# Revit family: Toilet-Elongated-Right_Height-American_Standard-Colony-221AB_Series
name_source: partatom
category: Plumbing Fixtures
revit_build: Autodesk Revit 2014 (Build: 20130308_1515(x64)
units: mm (PartAtom-declared; Revit-internal decimal feet)

## types (7) — shared parameters
ADA Compliant = Yes
Aquaguard Liner = No
Assembly Code = D2010110
Bowl Shape = Elongated
CW Connection = Yes
CWFU = 5
Cold Water Connection Diameter = 3/8"
Cold Water Connection Height = 10"
Cold Water Connection Radius = 3/16"
Cold Water Connection Width = 6"
Default Elevation = 0"
HW Connection = No
Height = 31"
Installation Type = Floor Mounted
Length = 27 13/16"
Manufacturer = American Standard
Price = Prices may vary. Please consult Manufacturer Representative for most up-to-date price list.
Product Documentation Link = https://www.americanstandard-us.com
Product Page URL = https://www.americanstandard-us.com
Revised Date = 01/14/2019
Type Comments = Available Finishes White, Bone, Linen
URL = http://www.americanstandard-us.com
Vent Connection = No
WFU = 5
Warranty Information = 2 Year Limited
Waste Connection = Yes
Waste Connection Diameter = 2"
Waste Connection Radius = 1"
Width = 18 11/16"
zero-valued in all types: HWFU

## per-type parameters (varying)
| type | Description | Finish | Flush Rate | Left Trip Lever | Material | Right Trip Lever |
| 221AB.104.020 | Colony HET Right Height Elongated 10 Inch Rough- In 1.28 gpf Toilet | Vitreous China-American Standard-020-White | 1.28 Gpf (4.8 Lpf) | Yes | Vitreous China-American Standard-020-White | No |
| 221AB.004.020 | Colony Right Height Elongated 10 Inch Rough- In 1.6 gpf Toilet | Vitreous China-American Standard-020-White | 1.6 gpf (6.0 Lpf) | Yes | Vitreous China-American Standard-020-White | No |
| 221AB.004.021 | Colony Right Height Elongated 10 Inch Rough- In 1.6 gpf Toilet | Vitreous China-American Standard-021-Bone | 1.6 gpf (6.0 Lpf) | Yes | Vitreous China-American Standard-021-Bone | No |
| 221AB.004.222 | Colony Right Height Elongated 10 Inch Rough- In 1.6 gpf Toilet | Vitreous China-American Standard-222-Linen | 1.6 gpf (6.0 Lpf) | Yes | Vitreous China-American Standard-222-Linen | No |
| 221AB.104.021 | Colony HET Right Height Elongated 10 Inch Rough- In 1.28 gpf Toilet | Vitreous China-American Standard-021-Bone | 1.28 Gpf (4.8 Lpf) | Yes | Vitreous China-American Standard-021-Bone | No |
| 221AB.104.222 | Colony HET Right Height Elongated 10 Inch Rough- In 1.28 gpf Toilet | Vitreous China-American Standard-222-Linen | 1.28 Gpf (4.8 Lpf) | Yes | Vitreous China-American Standard-222-Linen | No |
| 221AB.105.020 | Colony HET Right Height Elongated 10 Inch Rough- In 1.28 gpf Toilet | Vitreous China-American Standard-020-White | 1.28 Gpf (4.8 Lpf) | No | Vitreous China-American Standard-020-White | Yes |

note: column(s) folded — value = type name in every type: Model

## geometry (parser evidence)
native form markers: Sweep x1
no freeform markers — native parametric forms only
